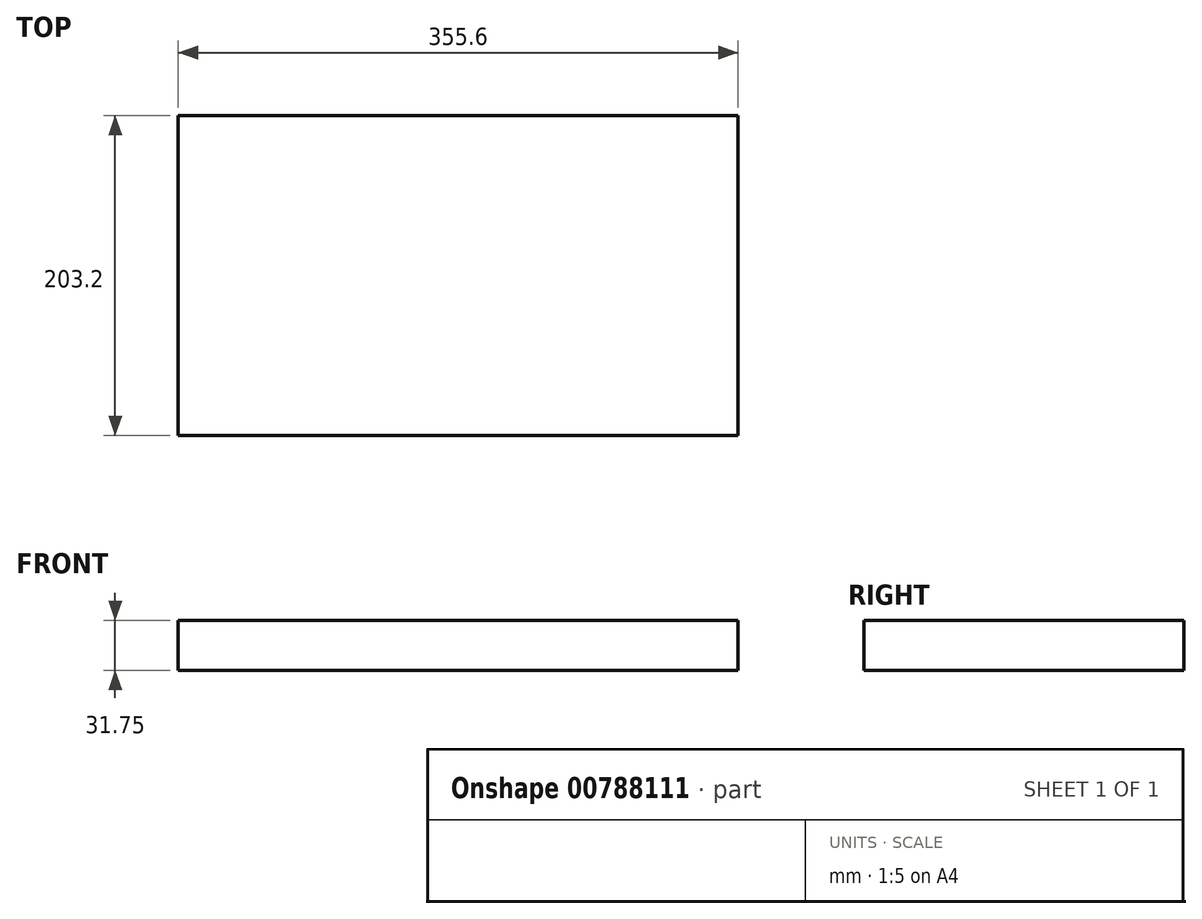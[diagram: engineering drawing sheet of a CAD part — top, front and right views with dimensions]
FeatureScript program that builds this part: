
annotation { "Feature Type Name" : "Feature", "Feature Type Description" : "" }
export const myFeature = defineFeature(function(context is Context, id is Id, definition is map)
    precondition{}
    {
        {
            var Q0;
            Q0=qCreatedBy(makeId("Top.planeOp"),FACE);
            var sketch = newSketch(context, id + "F0", { "sketchPlane" : qUnion([Q0])});
            skLineSegment(sketch, "E0.bottom", {"start": v(-49.47, -74) * mm, "end": v(306.13, -74) * mm});
            skLineSegment(sketch, "E0.left", {"start": v(-49.47, -74) * mm, "end": v(-49.47, 2669.2) * mm});
            skLineSegment(sketch, "E1.bottom", {"start": v(306.13, -74) * mm, "end": v(-49.47, -74) * mm});
            skLineSegment(sketch, "E1.top", {"start": v(306.13, 129.2) * mm, "end": v(-49.47, 129.2) * mm});
            skLineSegment(sketch, "E1.left", {"start": v(306.13, -74) * mm, "end": v(306.13, 129.2) * mm});
            skLineSegment(sketch, "E1.right", {"start": v(-49.47, -74) * mm, "end": v(-49.47, 129.2) * mm});
            skLineSegment(sketch, "E2.bottom", {"start": v(-49.47, 2669.2) * mm, "end": v(306.13, 2669.2) * mm});
            skLineSegment(sketch, "E2.top", {"start": v(-49.47, 2466) * mm, "end": v(306.13, 2466) * mm});
            skLineSegment(sketch, "E2.left", {"start": v(-49.47, 2669.2) * mm, "end": v(-49.47, 2466) * mm});
            skLineSegment(sketch, "E2.right", {"start": v(306.13, 2669.2) * mm, "end": v(306.13, 2466) * mm});
            skLineSegment(sketch, "E3.bottom", {"start": v(-49.47, 2466) * mm, "end": v(68.9, 2466) * mm});
            skLineSegment(sketch, "E3.top", {"start": v(-49.47, 129.2) * mm, "end": v(68.9, 129.2) * mm});
            skLineSegment(sketch, "E3.left", {"start": v(-49.47, 2466) * mm, "end": v(-49.47, 129.2) * mm});
            skLineSegment(sketch, "E3.right", {"start": v(68.9, 2466) * mm, "end": v(68.9, 129.2) * mm});
            skLineSegment(sketch, "E4.bottom", {"start": v(68.9, 2466) * mm, "end": v(187.26, 2466) * mm});
            skLineSegment(sketch, "E4.top", {"start": v(68.9, 129.2) * mm, "end": v(187.26, 129.2) * mm});
            skLineSegment(sketch, "E4.right", {"start": v(187.26, 2466) * mm, "end": v(187.26, 129.2) * mm});
            skLineSegment(sketch, "E5.bottom", {"start": v(187.26, 2466) * mm, "end": v(305.87, 2466) * mm});
            skLineSegment(sketch, "E5.top", {"start": v(187.26, 129.2) * mm, "end": v(305.87, 129.2) * mm});
            skLineSegment(sketch, "E5.right", {"start": v(305.87, 2466) * mm, "end": v(305.87, 129.2) * mm});
            skSolve(sketch);
        }
        {
            var Q0;
            Q0=makeQuery(id+"F0.imprint","IMPRINT",FACE,{"disambiguationData":[TD([[makeQuery(id+"F0.imprint","IMPRINT",EDGE,{"derivedFrom":sQuery(id+"F0.wireOp",EDGE,"E1.bottom")}),-1.0]])]});
            var Q1;
            Q1=makeQuery(id+"F0.imprint","IMPRINT",FACE,{"disambiguationData":[TD([[makeQuery(id+"F0.imprint","IMPRINT",EDGE,{"derivedFrom":sQuery(id+"F0.wireOp",EDGE,"hhWJXjZy-Gp1I-9ULU-i5Tf-SjkwVp0ApgQe.bottom")}),-1.0]])]});
            var Q2;
            Q2=makeQuery(id+"F0.imprint","IMPRINT",FACE,{"disambiguationData":[TD([[makeQuery(id+"F0.imprint","IMPRINT",EDGE,{"derivedFrom":sQuery(id+"F0.wireOp",EDGE,"B2HKc9pN-IzDt-xGxD-N7un-PIq4wqmvtq6E.bottom")}),-1.0]])]});
            var Q3;
            Q3=makeQuery(id+"F0.imprint","IMPRINT",FACE,{"disambiguationData":[TD([[makeQuery(id+"F0.imprint","IMPRINT",EDGE,{"derivedFrom":sQuery(id+"F0.wireOp",EDGE,"fpBT5Frx-vnzp-zUmu-zgOB-1pRn2kdQ02yE.bottom")}),-1.0]])]});
            var Q4;
            Q4=makeQuery(id+"F0.imprint","IMPRINT",FACE,{"disambiguationData":[TD([[makeQuery(id+"F0.imprint","IMPRINT",EDGE,{"derivedFrom":sQuery(id+"F0.wireOp",EDGE,"BCKM1Kho-uXB4-Vv4D-PQHz-iNvEprRD1uSd.bottom")}),-1.0]])]});
            var Q5;
            Q5=makeQuery(id+"F0.imprint","IMPRINT",FACE,{"disambiguationData":[TD([[makeQuery(id+"F0.imprint","IMPRINT",EDGE,{"derivedFrom":sQuery(id+"F0.wireOp",EDGE,"JSBFasWd-Hks5-IWBR-0bct-kklkx59penqr.bottom")}),-1.0]])]});
            var Q6;
            Q6=makeQuery(id+"F0.imprint","IMPRINT",FACE,{"disambiguationData":[TD([[makeQuery(id+"F0.imprint","IMPRINT",EDGE,{"derivedFrom":sQuery(id+"F0.wireOp",EDGE,"E5.bottom")}),-1.0]])]});
            var Q7;
            Q7=makeQuery(id+"F0.imprint","IMPRINT",FACE,{"disambiguationData":[TD([[makeQuery(id+"F0.imprint","IMPRINT",EDGE,{"derivedFrom":sQuery(id+"F0.wireOp",EDGE,"E4.bottom")}),-1.0]])]});
            var Q8;
            Q8=makeQuery(id+"F0.imprint","IMPRINT",FACE,{"disambiguationData":[TD([[makeQuery(id+"F0.imprint","IMPRINT",EDGE,{"derivedFrom":sQuery(id+"F0.wireOp",EDGE,"E3.bottom")}),-1.0]])]});
            var Q9;
            Q9=makeQuery(id+"F0.imprint","IMPRINT",FACE,{"disambiguationData":[TD([[makeQuery(id+"F0.imprint","IMPRINT",EDGE,{"derivedFrom":sQuery(id+"F0.wireOp",EDGE,"E2.bottom")}),-1.0]])]});
            extrude(context, id + "F1", {"entities" : qUnion([Q0, Q1, Q2, Q3, Q4, Q5, Q6, Q7, Q8, Q9]), "depth" : 31.75 * mm, "offsetDistance" : 25.4 * mm});
        }
    });
